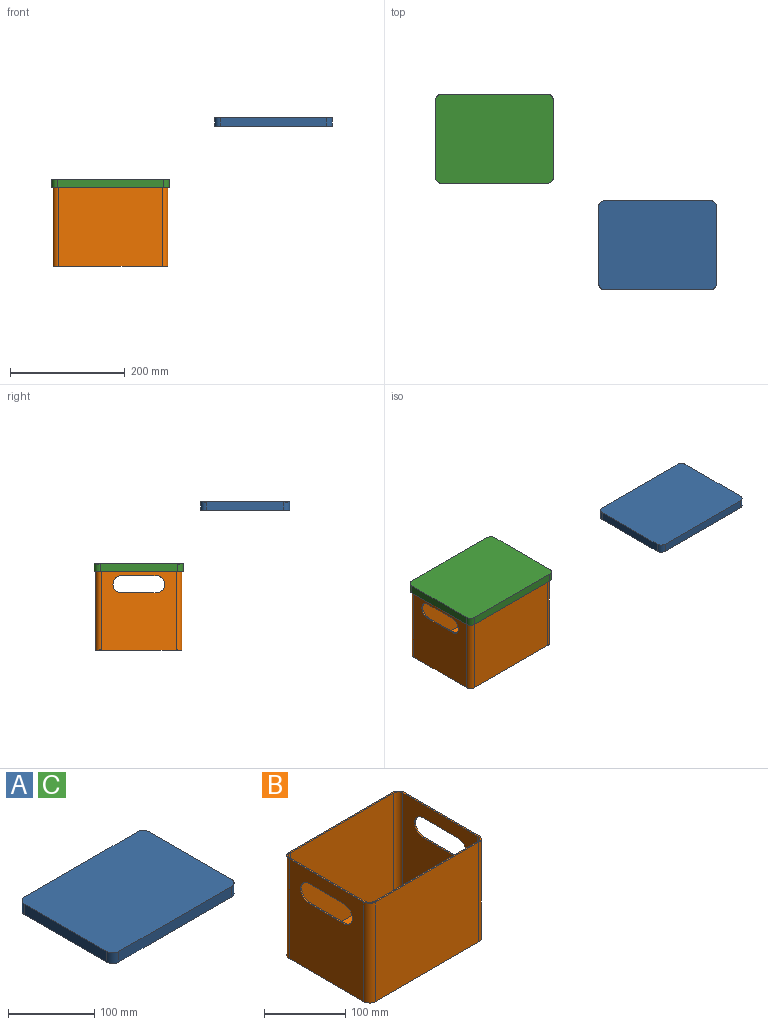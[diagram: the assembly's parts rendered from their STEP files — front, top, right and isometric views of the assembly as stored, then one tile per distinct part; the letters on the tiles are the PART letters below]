
ASSEMBLY  parts=3 mates=1
PART A: 19 faces, bbox 205x155x15 mm
  f0: plane 135x15mm, normal (1,0,0), area 2025mm2, adj f1,f7,f8,f9
  f1: cylinder r=10mm len=15mm, axis (0,0,-1), area 235.6mm2, adj f0,f2,f8,f9
  f2: plane 185x15mm, normal (0,1,0), area 2775mm2, adj f1,f3,f8,f9
  f3: cylinder r=10mm len=15mm, axis (0,0,-1), area 235.6mm2, adj f2,f4,f8,f9
  f4: plane 135x15mm, normal (-1,0,0), area 2025mm2, adj f3,f5,f8,f9
  f5: cylinder r=10mm len=15mm, axis (0,0,-1), area 235.6mm2, adj f4,f6,f8,f9
  f6: plane 185x15mm, normal (0,-1,0), area 2775mm2, adj f5,f7,f8,f9
  f7: cylinder r=10mm len=15mm, axis (0,0,-1), area 235.6mm2, adj f0,f6,f8,f9
  f8: plane 205x155mm, normal (0,0,1), area 31689.2mm2, adj f0,f1,f2,f3,f4,f5,f6,f7
  f9: plane 205x155mm, normal (0,0,-1), area 1393.1mm2, adj f0,f1,f2,f3,f4,f5,f6,f7
  f10: plane 135x13mm, normal (-1,0,0), area 1755mm2, adj f9,f11,f17,f18
  f11: cylinder r=8mm len=13mm, axis (0,0,-1), area 163.4mm2, adj f9,f10,f12,f18
  f12: plane 185x13mm, normal (0,-1,0), area 2405mm2, adj f9,f11,f13,f18
  f13: cylinder r=8mm len=13mm, axis (0,0,-1), area 163.4mm2, adj f9,f12,f14,f18
  f14: plane 135x13mm, normal (1,0,0), area 1755mm2, adj f9,f13,f15,f18
  f15: cylinder r=8mm len=13mm, axis (0,0,-1), area 163.4mm2, adj f9,f14,f16,f18
  f16: plane 185x13mm, normal (0,1,0), area 2405mm2, adj f9,f15,f17,f18
  f17: cylinder r=8mm len=13mm, axis (0,0,-1), area 163.4mm2, adj f9,f10,f16,f18
  f18: plane 201x151mm, normal (0,0,-1), area 30296.1mm2, adj f10,f11,f12,f13,f14,f15,f16,f17
PART B: 27 faces, bbox 200x150x150 mm
  f0: plane 150x130mm, normal (-1,0,0), area 16993.1mm2, adj f5,f6,f10,f11,f23,f24,f25,f26
  f1: plane 150x130mm, normal (1,0,0), area 16993.1mm2, adj f8,f9,f10,f11,f19,f20,f21,f22
  f2: plane 148x130mm, normal (1,0,0), area 16733.1mm2, adj f10,f13,f14,f18,f23,f24,f25,f26
  f3: plane 148x130mm, normal (-1,0,0), area 16733.1mm2, adj f10,f16,f17,f18,f19,f20,f21,f22
  f4: plane 180x150mm, normal (0,1,0), area 27000mm2, adj f5,f9,f10,f11
  f5: cylinder r=10mm len=150mm, axis (0,0,-1), area 2356.2mm2, adj f0,f4,f10,f11
  f6: cylinder r=10mm len=150mm, axis (0,0,-1), area 2356.2mm2, adj f0,f7,f10,f11
  f7: plane 180x150mm, normal (0,-1,0), area 27000mm2, adj f6,f8,f10,f11
  f8: cylinder r=10mm len=150mm, axis (0,0,-1), area 2356.2mm2, adj f1,f7,f10,f11
  f9: cylinder r=10mm len=150mm, axis (0,0,-1), area 2356.2mm2, adj f1,f4,f10,f11
  f10: plane 200x150mm, normal (0,0,1), area 1353.1mm2, adj f0,f1,f2,f3,f4,f5,f6,f7
  f11: plane 200x150mm, normal (0,0,-1), area 29914.2mm2, adj f0,f1,f4,f5,f6,f7,f8,f9
  f12: plane 180x148mm, normal (0,-1,0), area 26640mm2, adj f10,f13,f17,f18
  f13: cylinder r=8mm len=148mm, axis (0,0,-1), area 1859.8mm2, adj f2,f10,f12,f18
  f14: cylinder r=8mm len=148mm, axis (0,0,-1), area 1859.8mm2, adj f2,f10,f15,f18
  f15: plane 180x148mm, normal (0,1,0), area 26640mm2, adj f10,f14,f16,f18
  f16: cylinder r=8mm len=148mm, axis (0,0,-1), area 1859.8mm2, adj f3,f10,f15,f18
  f17: cylinder r=8mm len=148mm, axis (0,0,-1), area 1859.8mm2, adj f3,f10,f12,f18
  f18: plane 196x146mm, normal (0,0,1), area 28561.1mm2, adj f2,f3,f12,f13,f14,f15,f16,f17
  f19: plane 60x2mm, normal (0,0,1), area 120mm2, adj f1,f3,f20,f22
  f20: cylinder r=15mm len=30mm, axis (-1,0,0), area 94.2mm2, adj f1,f3,f19,f21
  f21: plane 60x2mm, normal (0,0,-1), area 120mm2, adj f1,f3,f20,f22
  f22: cylinder r=15mm len=30mm, axis (-1,0,0), area 94.2mm2, adj f1,f3,f19,f21
  f23: cylinder r=15mm len=30mm, axis (-1,0,0), area 94.2mm2, adj f0,f2,f24,f26
  f24: plane 60x2mm, normal (0,0,-1), area 120mm2, adj f0,f2,f23,f25
  f25: cylinder r=15mm len=30mm, axis (-1,0,0), area 94.2mm2, adj f0,f2,f24,f26
  f26: plane 60x2mm, normal (0,0,1), area 120mm2, adj f0,f2,f23,f25
PART C: same geometry as A
PLACE A at identity
PLACE B t=(-283.92,185.25,-176.45)mm
PLACE C t=(-283.92,185.25,-106.95)mm
MATE fastened C.f18 <-> B.f10  axis (0,0,-1) through (-283.92,185.25,-101.45)mm
